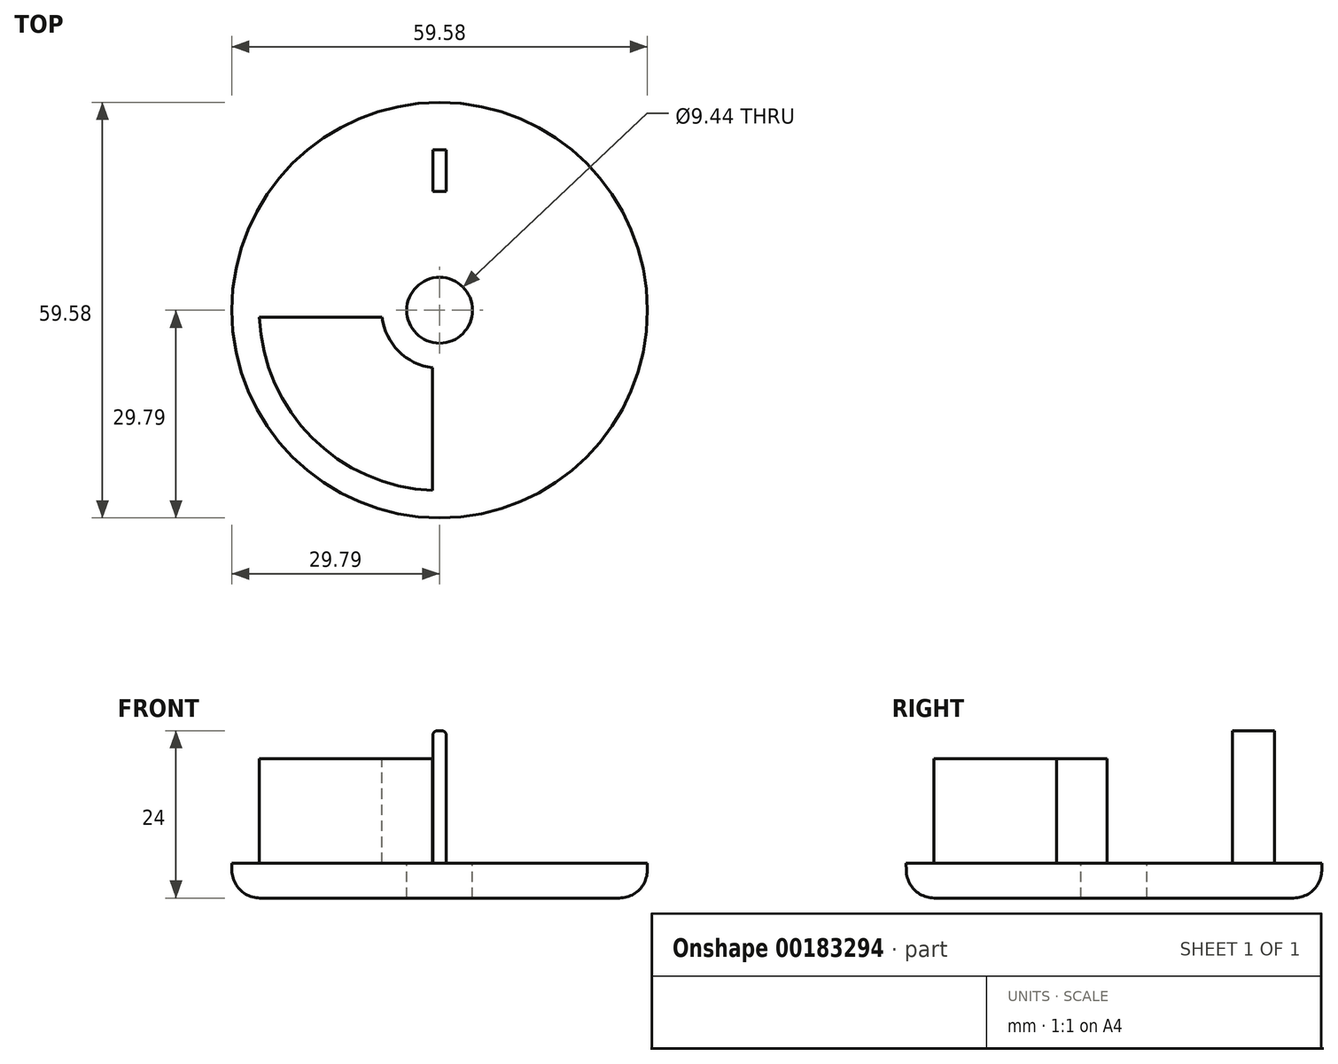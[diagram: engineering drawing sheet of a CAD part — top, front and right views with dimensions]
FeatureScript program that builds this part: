
annotation { "Feature Type Name" : "Feature", "Feature Type Description" : "" }
export const myFeature = defineFeature(function(context is Context, id is Id, definition is map)
    precondition{}
    {
        {
            var Q0;
            Q0=qCreatedBy(makeId("Front.planeOp"),FACE);
            var sketch = newSketch(context, id + "F0", { "sketchPlane" : qUnion([Q0]), "disableImprinting" : false});
            skLineSegment(sketch, "E0", {"start": v(-30, 20) * mm, "end": v(-2, 20) * mm});
            skLineSegment(sketch, "E1", {"start": v(-2, 20) * mm, "end": v(-2, 16) * mm});
            skLineSegment(sketch, "E2", {"start": v(-2, 16) * mm, "end": v(-4.72, 16) * mm});
            skLineSegment(sketch, "E3", {"start": v(-4.72, 16) * mm, "end": v(-4.72, 0) * mm});
            skLineSegment(sketch, "E4", {"start": v(-4.72, 0) * mm, "end": v(-25.77, 0) * mm});
            skLineSegment(sketch, "E5", {"start": v(-29.77, 3.94) * mm, "end": v(-30, 20) * mm});
            skLineSegment(sketch, "E6", {"start": v(0, 14.85) * mm, "end": v(0, -1.46) * mm, "construction": true});
            skPoint(sketch, "E7.visualSharp", {"position": v(-29.72, 0) * mm});
            skArc(sketch, "E7.filletArc", {"start": v(-29.77, 3.94) * mm, "mid": v(-28.58, 1.15) * mm, "end": v(-25.77, 0) * mm});
            skSolve(sketch);
        }
        {
            var Q0;
            Q0=makeQuery(id+"F0.imprint","IMPRINT",FACE,{"disambiguationData":[TD([[makeQuery(id+"F0.imprint","IMPRINT",EDGE,{"derivedFrom":sQuery(id+"F0.wireOp",EDGE,"E0")}),-1.0]])]});
            var Q1;
            Q1=sQuery(id+"F0.wireOp",EDGE,"E6");
            revolve(context, id + "F1", {"surfaceOperationType" : NewSurfaceOperationType.NEW, "entities" : qUnion([Q0]), "thickness1" : 5 * mm, "thickness2" : 0 * mm, "thickness" : 5 * mm, "axis" : qUnion([Q1]), "revolveType" : RevolveType.FULL});
        }
        {
            var Q0;
            Q0=makeQuery(id+"F1.opRevolve","SWEPT_FACE",FACE,{"disambiguationData":[OSD([sQuery(id+"F0.wireOp",EDGE,"E0")])]});
            var sketch = newSketch(context, id + "F2", { "sketchPlane" : qUnion([Q0]), "disableImprinting" : false});
            skCircle(sketch, "E8.0", {"center": v(0, 0) * mm, "radius": 2 * mm});
            skArc(sketch, "E9", {"start": v(-1, -8.25) * mm, "mid": v(-5.88, -5.88) * mm, "end": v(-8.25, -1) * mm});
            skLineSegment(sketch, "E10", {"start": v(-8.25, -1) * mm, "end": v(-25.84, -1) * mm});
            skArc(sketch, "E11", {"start": v(-25.84, -1) * mm, "mid": v(-18.29, -18.29) * mm, "end": v(-1, -25.84) * mm});
            skLineSegment(sketch, "E12", {"start": v(-1, -8.25) * mm, "end": v(-1, -25.84) * mm});
            skLineSegment(sketch, "E13", {"start": v(-13.99, 0) * mm, "end": v(13.44, 0) * mm, "construction": true});
            skLineSegment(sketch, "E14", {"start": v(0, -12.97) * mm, "end": v(0, 11.95) * mm, "construction": true});
            skLineSegment(sketch, "E15.1.0", {"start": v(0.93, -8.28) * mm, "end": v(0.93, -25.87) * mm});
            skArc(sketch, "E15.1.1", {"start": v(8.18, -1.03) * mm, "mid": v(5.8, -5.9) * mm, "end": v(0.93, -8.28) * mm});
            skLineSegment(sketch, "E15.1.2", {"start": v(8.18, -1.03) * mm, "end": v(25.77, -1.03) * mm});
            skArc(sketch, "E15.1.3", {"start": v(0.93, -25.87) * mm, "mid": v(18.22, -18.31) * mm, "end": v(25.77, -1.03) * mm});
            skLineSegment(sketch, "E15.2.0", {"start": v(8.2, 0.9) * mm, "end": v(25.8, 0.9) * mm});
            skArc(sketch, "E15.2.1", {"start": v(0.96, 8.16) * mm, "mid": v(5.83, 5.78) * mm, "end": v(8.2, 0.9) * mm});
            skLineSegment(sketch, "E15.2.2", {"start": v(0.96, 8.16) * mm, "end": v(0.96, 25.75) * mm});
            skArc(sketch, "E15.2.3", {"start": v(25.8, 0.9) * mm, "mid": v(18.25, 18.2) * mm, "end": v(0.96, 25.75) * mm});
            skLineSegment(sketch, "E15.3.0", {"start": v(-0.97, 8.18) * mm, "end": v(-0.97, 25.77) * mm});
            skArc(sketch, "E15.3.1", {"start": v(-8.23, 0.93) * mm, "mid": v(-5.85, 5.8) * mm, "end": v(-0.97, 8.18) * mm});
            skLineSegment(sketch, "E15.3.2", {"start": v(-8.23, 0.93) * mm, "end": v(-25.82, 0.93) * mm});
            skArc(sketch, "E15.3.3", {"start": v(-0.97, 25.77) * mm, "mid": v(-18.26, 18.22) * mm, "end": v(-25.82, 0.93) * mm});
            skPoint(sketch, "E15.center", {"position": v(-0.02, -0.05) * mm});
            skLineSegment(sketch, "E16", {"start": v(-0.97, 17) * mm, "end": v(0.96, 17) * mm});
            skLineSegment(sketch, "E17", {"start": v(-0.97, 23) * mm, "end": v(0.96, 23) * mm});
            skSolve(sketch);
        }
        {
            var Q0;
            Q0=makeQuery(id+"F2.imprint","IMPRINT",FACE,{"disambiguationData":[TD([[makeQuery(id+"F2.imprint","IMPRINT",EDGE,{"derivedFrom":sQuery(id+"F2.wireOp",EDGE,"E9")}),1.0]])]});
            var Q1;
            Q1=makeQuery(id+"F2.imprint","IMPRINT",FACE,{"disambiguationData":[TD([[makeQuery(id+"F2.imprint","IMPRINT",EDGE,{"derivedFrom":sQuery(id+"F2.wireOp",EDGE,"E15.1.0")}),1.0]])]});
            var Q2;
            Q2=makeQuery(id+"F2.imprint","IMPRINT",FACE,{"disambiguationData":[TD([[makeQuery(id+"F2.imprint","IMPRINT",EDGE,{"derivedFrom":sQuery(id+"F2.wireOp",EDGE,"E15.2.0")}),1.0]])]});
            var Q3;
            Q3=makeQuery(id+"F2.imprint","IMPRINT",FACE,{"disambiguationData":[TD([[makeQuery(id+"F2.imprint","IMPRINT",EDGE,{"derivedFrom":sQuery(id+"F2.wireOp",EDGE,"E15.3.0")}),1.0]])]});
            extrude(context, id + "F3", {"entities" : qUnion([Q0, Q1, Q2, Q3]), "operationType" : NewBodyOperationType.REMOVE, "flatOperationType" : FlatOperationType.REMOVE, "thickness1" : 5 * mm, "thickness2" : 0 * mm, "thickness" : 5 * mm, "oppositeDirection" : true, "offsetDistance" : 25 * mm, "startOffsetBound" : StartOffsetType.BLIND, "startOffsetDistance" : 25 * mm, "depth" : 15 * mm, "domain" : OperationDomain.MODEL});
        }
        {
            var Q0;
            {var subQ0=sQuery(id+"F2.wireOp",EDGE,"E16");Q0=makeQuery(id+"F2.imprint","IMPRINT",FACE,{"disambiguationData":[TD([[makeQuery(id+"F2.imprint","IMPRINT",EDGE,{"derivedFrom":subQ0}),1.0]])]});}
            extrude(context, id + "F4", {"entities" : qUnion([Q0]), "operationType" : NewBodyOperationType.ADD, "depth" : 4 * mm});
        }
        {
            var Q0;
            Q0=makeQuery(id+"F4.opExtrude","CAP_EDGE",EDGE,{"disambiguationData":[OSD([sQuery(id+"F2.wireOp",EDGE,"E15.3.0")])],"isStart":false});
            fillet(context, id + "F5", {"entities" : qUnion([Q0]), "radius" : 0.7 * mm, "tangentPropagation" : true, "allowEdgeOverflow" : false});
        }
        {
            var Q0;
            Q0=makeQuery(id+"F4.opExtrude","CAP_EDGE",EDGE,{"disambiguationData":[OSD([sQuery(id+"F2.wireOp",EDGE,"E15.2.2")])],"isStart":false});
            fillet(context, id + "F6", {"entities" : qUnion([Q0]), "radius" : 0.7 * mm, "tangentPropagation" : true, "allowEdgeOverflow" : false});
        }
    });
